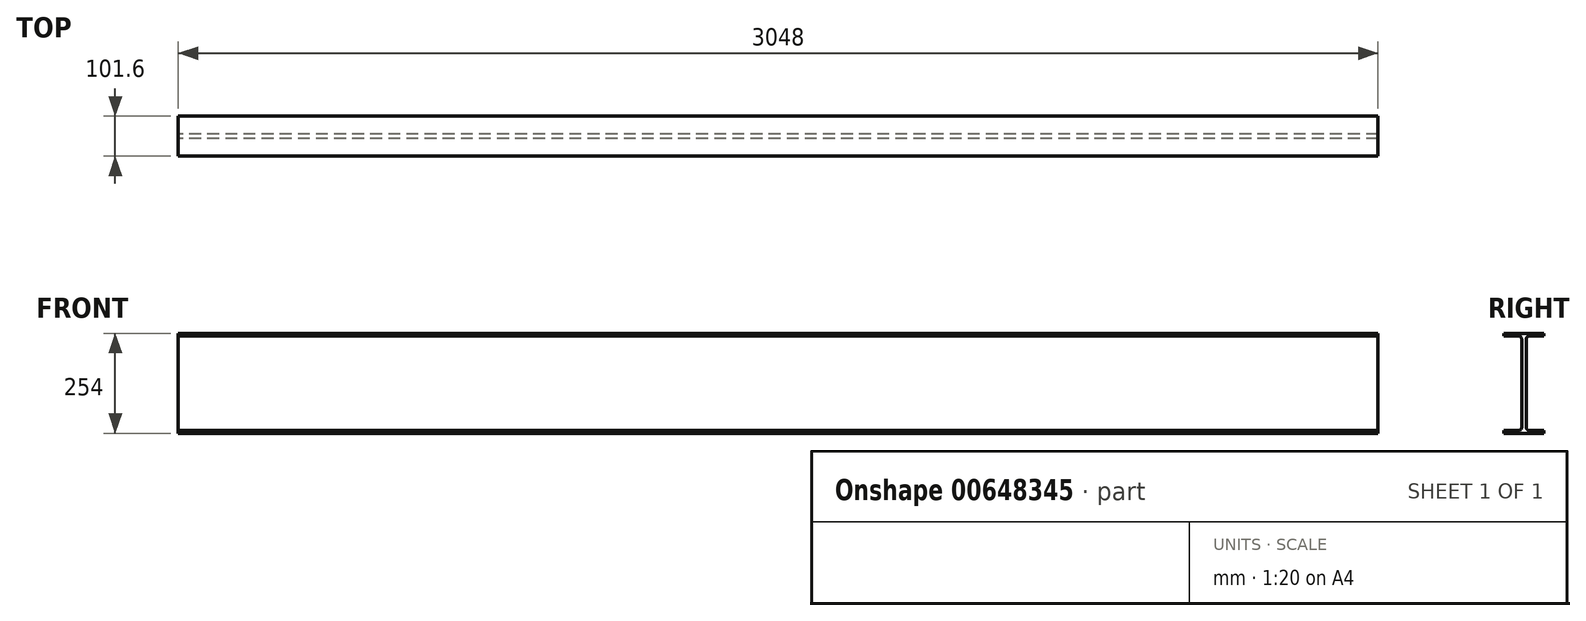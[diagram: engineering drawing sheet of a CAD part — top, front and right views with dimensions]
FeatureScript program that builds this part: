
annotation { "Feature Type Name" : "Feature", "Feature Type Description" : "" }
export const myFeature = defineFeature(function(context is Context, id is Id, definition is map)
    precondition{}
    {
        {
            var Q0;
            Q0=qCreatedBy(makeId("Right.planeOp"),FACE);
            var sketch = newSketch(context, id + "F0", { "sketchPlane" : qUnion([Q0])});
            skLineSegment(sketch, "E0", {"start": v(-5.84, 0) * mm, "end": v(-5.84, 112.23) * mm});
            skLineSegment(sketch, "E1", {"start": v(-13.78, 120.17) * mm, "end": v(-50.8, 120.17) * mm});
            skLineSegment(sketch, "E2", {"start": v(-50.8, 120.17) * mm, "end": v(-50.8, 127) * mm});
            skLineSegment(sketch, "E3", {"start": v(-50.8, 127) * mm, "end": v(0, 127) * mm});
            skPoint(sketch, "E4.visualSharp", {"position": v(-5.84, 120.17) * mm});
            skArc(sketch, "E4.filletArc", {"start": v(-5.84, 112.23) * mm, "mid": v(-8.17, 117.84) * mm, "end": v(-13.78, 120.17) * mm});
            skLineSegment(sketch, "E5.MirrorCS", {"start": v(5.84, 0) * mm, "end": v(5.84, 112.23) * mm});
            skPoint(sketch, "E6.MirrorP", {"position": v(5.84, 120.17) * mm});
            skLineSegment(sketch, "E7.MirrorCS", {"start": v(13.78, 120.17) * mm, "end": v(50.8, 120.17) * mm});
            skArc(sketch, "E8.MirrorCS", {"start": v(5.84, 112.23) * mm, "mid": v(8.17, 117.84) * mm, "end": v(13.78, 120.17) * mm});
            skLineSegment(sketch, "E9.MirrorCS", {"start": v(50.8, 127) * mm, "end": v(0, 127) * mm});
            skLineSegment(sketch, "E10.MirrorCS", {"start": v(50.8, 120.17) * mm, "end": v(50.8, 127) * mm});
            skLineSegment(sketch, "E11.MirrorCS", {"start": v(50.8, -120.17) * mm, "end": v(50.8, -127) * mm});
            skLineSegment(sketch, "E12.MirrorCS", {"start": v(-50.8, -120.17) * mm, "end": v(-50.8, -127) * mm});
            skArc(sketch, "E13.MirrorCS", {"start": v(5.84, -112.23) * mm, "mid": v(8.17, -117.84) * mm, "end": v(13.78, -120.17) * mm});
            skArc(sketch, "E14.MirrorCS", {"start": v(-5.84, -112.23) * mm, "mid": v(-8.17, -117.84) * mm, "end": v(-13.78, -120.17) * mm});
            skLineSegment(sketch, "E15.MirrorCS", {"start": v(-5.84, 0) * mm, "end": v(-5.84, -112.23) * mm});
            skPoint(sketch, "E16.MirrorP", {"position": v(5.84, -120.17) * mm});
            skLineSegment(sketch, "E17.MirrorCS", {"start": v(-13.78, -120.17) * mm, "end": v(-50.8, -120.17) * mm});
            skPoint(sketch, "E18.MirrorP", {"position": v(-5.84, -120.17) * mm});
            skLineSegment(sketch, "E19.MirrorCS", {"start": v(-50.8, -127) * mm, "end": v(0, -127) * mm});
            skLineSegment(sketch, "E20.MirrorCS", {"start": v(13.78, -120.17) * mm, "end": v(50.8, -120.17) * mm});
            skLineSegment(sketch, "E21.MirrorCS", {"start": v(50.8, -127) * mm, "end": v(0, -127) * mm});
            skLineSegment(sketch, "E22.MirrorCS", {"start": v(5.84, 0) * mm, "end": v(5.84, -112.23) * mm});
            skSolve(sketch);
        }
        {
            var Q0;
            Q0=makeQuery(id+"F0.imprint","IMPRINT",FACE,{"disambiguationData":[TD([[makeQuery(id+"F0.imprint","IMPRINT",EDGE,{"derivedFrom":sQuery(id+"F0.wireOp",EDGE,"E0")}),-1.0]])]});
            extrude(context, id + "F1", {"entities" : qUnion([Q0]), "depth" : 3048 * mm, "offsetDistance" : 25.4 * mm});
        }
    });
